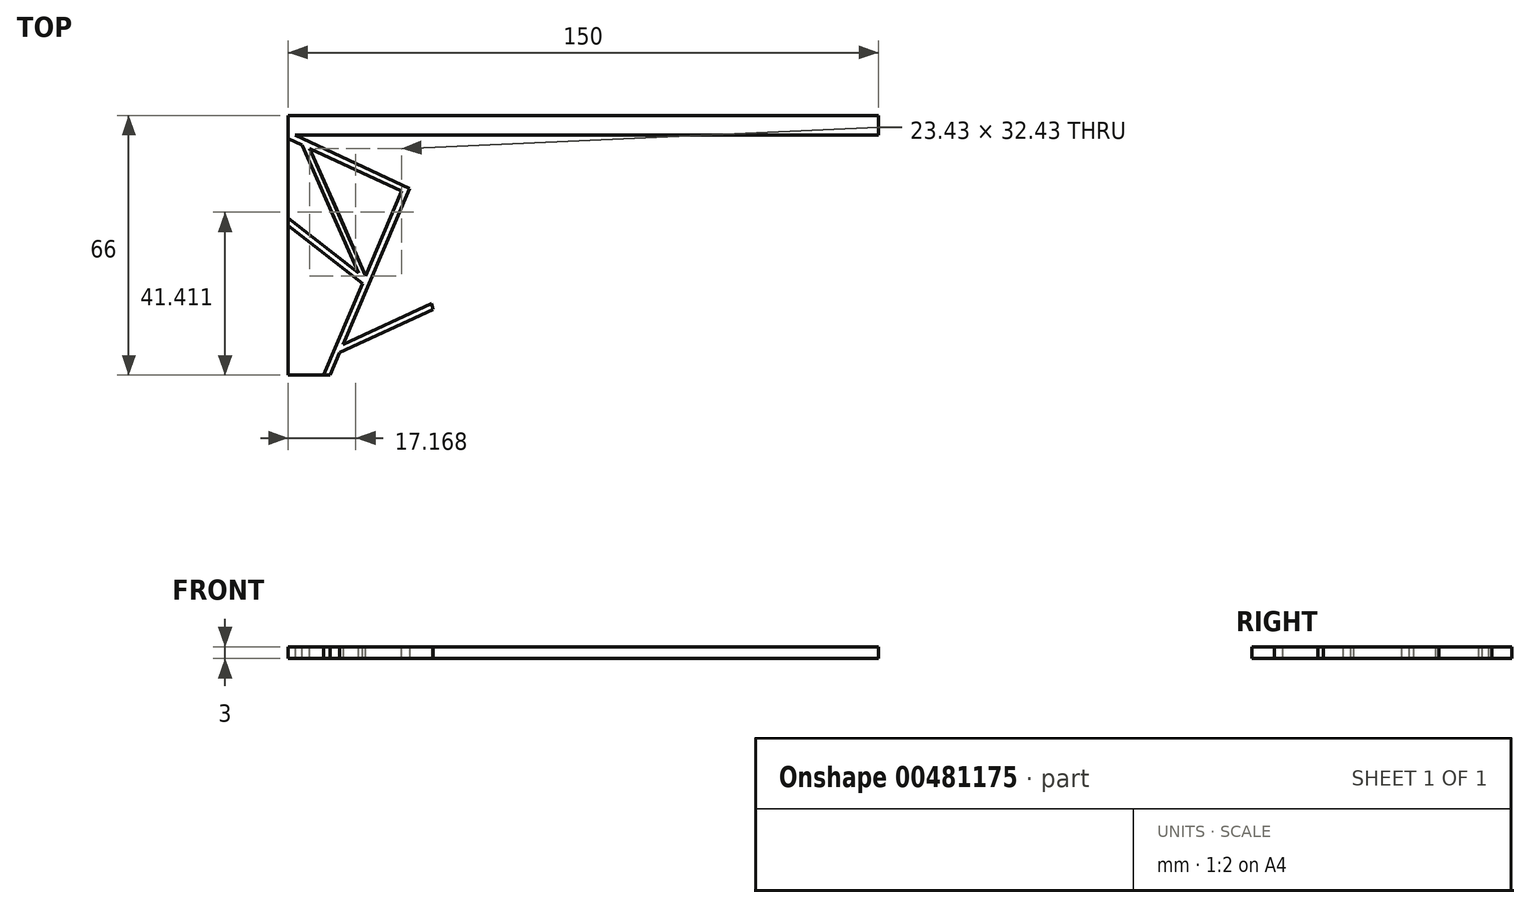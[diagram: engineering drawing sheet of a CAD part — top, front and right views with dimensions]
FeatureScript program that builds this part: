
annotation { "Feature Type Name" : "Feature", "Feature Type Description" : "" }
export const myFeature = defineFeature(function(context is Context, id is Id, definition is map)
    precondition{}
    {
        {
            var Q0;
            Q0=qCreatedBy(makeId("Top.planeOp"),FACE);
            var sketch = newSketch(context, id + "F0", { "sketchPlane" : qUnion([Q0])});
            skLineSegment(sketch, "E0", {"start": v(-52.18, 35.99) * mm, "end": v(-52.18, -44.01) * mm});
            skLineSegment(sketch, "E1", {"start": v(-52.18, -44.01) * mm, "end": v(27.82, -44.01) * mm});
            skLineSegment(sketch, "E2.bottom", {"start": v(-52.18, 35.99) * mm, "end": v(107.82, 35.99) * mm});
            skLineSegment(sketch, "E2.top", {"start": v(-52.18, -44.01) * mm, "end": v(107.82, -44.01) * mm});
            skLineSegment(sketch, "E2.right", {"start": v(107.82, 35.99) * mm, "end": v(107.82, -44.01) * mm});
            skLineSegment(sketch, "E3", {"start": v(-52.18, 35.99) * mm, "end": v(-52.18, 26.99) * mm});
            skLineSegment(sketch, "E4", {"start": v(-52.18, 26.99) * mm, "end": v(107.82, 26.99) * mm});
            skLineSegment(sketch, "E5.bottom", {"start": v(-52.18, 26.99) * mm, "end": v(-47.18, 26.99) * mm});
            skLineSegment(sketch, "E5.top", {"start": v(-52.18, -44.01) * mm, "end": v(-47.18, -44.01) * mm});
            skLineSegment(sketch, "E5.left", {"start": v(-52.18, 26.99) * mm, "end": v(-52.18, -44.01) * mm});
            skLineSegment(sketch, "E5.right", {"start": v(-47.18, 26.99) * mm, "end": v(-47.18, -44.01) * mm});
            skLineSegment(sketch, "E6.bottom", {"start": v(107.82, 26.99) * mm, "end": v(102.82, 26.99) * mm});
            skLineSegment(sketch, "E6.top", {"start": v(107.82, -44.01) * mm, "end": v(102.82, -44.01) * mm});
            skLineSegment(sketch, "E6.left", {"start": v(107.82, 26.99) * mm, "end": v(107.82, -44.01) * mm});
            skLineSegment(sketch, "E6.right", {"start": v(102.82, 26.99) * mm, "end": v(102.82, -44.01) * mm});
            skLineSegment(sketch, "E7.top", {"start": v(-52.18, 21.99) * mm, "end": v(107.82, 21.99) * mm});
            skLineSegment(sketch, "E7.left", {"start": v(-52.18, 26.99) * mm, "end": v(-52.18, 21.99) * mm});
            skLineSegment(sketch, "E7.right", {"start": v(107.82, 26.99) * mm, "end": v(107.82, 21.99) * mm});
            skLineSegment(sketch, "E8.top", {"start": v(-52.18, -39.01) * mm, "end": v(107.82, -39.01) * mm});
            skLineSegment(sketch, "E8.left", {"start": v(-52.18, -44.01) * mm, "end": v(-52.18, -39.01) * mm});
            skLineSegment(sketch, "E8.right", {"start": v(107.82, -44.01) * mm, "end": v(107.82, -39.01) * mm});
            skLineSegment(sketch, "E9", {"start": v(-47.18, 21.99) * mm, "end": v(0, 0) * mm});
            skLineSegment(sketch, "E10", {"start": v(0, 0) * mm, "end": v(11.28, 21.99) * mm});
            skLineSegment(sketch, "E11", {"start": v(11.28, 21.99) * mm, "end": v(23.62, -10.68) * mm});
            skLineSegment(sketch, "E12", {"start": v(23.62, -10.68) * mm, "end": v(-8.56, -30.37) * mm});
            skLineSegment(sketch, "E13", {"start": v(-8.56, -30.37) * mm, "end": v(-17.33, 8.07) * mm});
            skLineSegment(sketch, "E14", {"start": v(-17.33, 8.07) * mm, "end": v(-37.35, -39.01) * mm});
            skLineSegment(sketch, "E15", {"start": v(-37.35, -39.01) * mm, "end": v(42.87, -39.01) * mm});
            skLineSegment(sketch, "E16", {"start": v(42.87, -39.01) * mm, "end": v(7.53, -20.53) * mm});
            skLineSegment(sketch, "E17", {"start": v(102.82, -20.53) * mm, "end": v(74.6, 0) * mm});
            skLineSegment(sketch, "E18", {"start": v(74.6, 0) * mm, "end": v(42.87, -39.01) * mm});
            skLineSegment(sketch, "E19", {"start": v(57.9, -20.53) * mm, "end": v(31.89, 21.99) * mm});
            skLineSegment(sketch, "E20", {"start": v(31.89, 21.99) * mm, "end": v(45.34, 0) * mm});
            skLineSegment(sketch, "E21", {"start": v(45.34, 0) * mm, "end": v(95.17, 21.99) * mm});
            skLineSegment(sketch, "E22", {"start": v(95.17, 21.99) * mm, "end": v(86.96, -9) * mm});
            skPoint(sketch, "E23.endSnap0", {"position": v(38.62, 11) * mm});
            skLineSegment(sketch, "E24", {"start": v(75, -20.53) * mm, "end": v(81.37, -30.93) * mm});
            skLineSegment(sketch, "E25", {"start": v(81.37, -30.93) * mm, "end": v(96.81, -39.01) * mm});
            skLineSegment(sketch, "E26", {"start": v(-27.34, -15.47) * mm, "end": v(-47.18, 0) * mm});
            skLineSegment(sketch, "E27", {"start": v(-23.59, 11) * mm, "end": v(-23.27, 11.67) * mm});
            skLineSegment(sketch, "E28", {"start": v(-23.59, 11) * mm, "end": v(-23.9, 10.31) * mm});
            skLineSegment(sketch, "E29", {"start": v(-23.27, 11.67) * mm, "end": v(-45.4, 21.99) * mm});
            skLineSegment(sketch, "E30", {"start": v(-23.9, 10.31) * mm, "end": v(-47.18, 21.16) * mm});
            skLineSegment(sketch, "E31", {"start": v(-23.9, 10.31) * mm, "end": v(0, -0.83) * mm});
            skLineSegment(sketch, "E32", {"start": v(-23.27, 11.67) * mm, "end": v(0.34, 0.67) * mm});
            skLineSegment(sketch, "E33", {"start": v(-22.37, -3.79) * mm, "end": v(-23.05, -3.47) * mm});
            skLineSegment(sketch, "E34", {"start": v(-22.37, -3.79) * mm, "end": v(-21.68, -4.08) * mm});
            skLineSegment(sketch, "E35", {"start": v(-23.05, -3.47) * mm, "end": v(-17.71, 9.08) * mm});
            skLineSegment(sketch, "E36", {"start": v(-21.68, -4.08) * mm, "end": v(-16.35, 8.45) * mm});
            skLineSegment(sketch, "E37", {"start": v(-21.68, -4.08) * mm, "end": v(-36.54, -39.01) * mm});
            skLineSegment(sketch, "E38", {"start": v(-23.05, -3.47) * mm, "end": v(-38.17, -39.01) * mm});
            skLineSegment(sketch, "E39", {"start": v(-37.26, -7.73) * mm, "end": v(-36.8, -7.14) * mm});
            skLineSegment(sketch, "E40", {"start": v(-37.26, -7.73) * mm, "end": v(-37.72, -8.33) * mm});
            skLineSegment(sketch, "E41", {"start": v(-36.8, -7.14) * mm, "end": v(-47.18, 0.95) * mm});
            skLineSegment(sketch, "E42", {"start": v(-47.18, 0.95) * mm, "end": v(-27.04, -14.75) * mm});
            skLineSegment(sketch, "E43", {"start": v(-37.72, -8.33) * mm, "end": v(-47.18, -0.95) * mm});
            skLineSegment(sketch, "E44", {"start": v(-37.72, -8.33) * mm, "end": v(-28.26, -15.7) * mm});
            skLineSegment(sketch, "E45", {"start": v(-8.56, -39.01) * mm, "end": v(-8.56, -30.37) * mm});
            skLineSegment(sketch, "E46", {"start": v(81.37, -30.93) * mm, "end": v(64.21, -39.01) * mm});
            skLineSegment(sketch, "E47", {"start": v(63.35, 21.99) * mm, "end": v(66.4, 9.29) * mm});
            skLineSegment(sketch, "E48", {"start": v(64.21, -39.01) * mm, "end": v(51.37, -28.56) * mm});
            skLineSegment(sketch, "E49", {"start": v(-33.66, -32.25) * mm, "end": v(-10.57, -21.53) * mm});
            skLineSegment(sketch, "E50", {"start": v(57.9, -20.53) * mm, "end": v(17.7, -14.3) * mm});
            skLineSegment(sketch, "E51", {"start": v(75, -20.53) * mm, "end": v(82.14, -5.48) * mm});
            skLineSegment(sketch, "E52", {"start": v(82.14, -5.48) * mm, "end": v(75, -20.53) * mm});
            skLineSegment(sketch, "E53", {"start": v(75, -20.53) * mm, "end": v(102.82, -28.16) * mm});
            skLineSegment(sketch, "E54", {"start": v(-22.12, -26.89) * mm, "end": v(-22.43, -26.2) * mm});
            skLineSegment(sketch, "E55", {"start": v(-22.43, -26.2) * mm, "end": v(-10.74, -20.78) * mm});
            skLineSegment(sketch, "E56", {"start": v(-22.43, -26.2) * mm, "end": v(-33.22, -31.22) * mm});
            skLineSegment(sketch, "E57", {"start": v(-22.12, -26.89) * mm, "end": v(-21.8, -27.57) * mm});
            skLineSegment(sketch, "E58", {"start": v(-21.8, -27.57) * mm, "end": v(-10.4, -22.28) * mm});
            skLineSegment(sketch, "E59", {"start": v(-21.8, -27.57) * mm, "end": v(-34.1, -33.28) * mm});
            skLineSegment(sketch, "E60", {"start": v(75, -20.53) * mm, "end": v(67.3, -8.98) * mm});
            skLineSegment(sketch, "E61", {"start": v(18.1, 3.95) * mm, "end": v(38.62, 11) * mm});
            skLineSegment(sketch, "E62", {"start": v(7.53, -20.53) * mm, "end": v(0, 0) * mm});
            skLineSegment(sketch, "E63", {"start": v(-16.35, 8.45) * mm, "end": v(0, 21.99) * mm});
            skLineSegment(sketch, "E64", {"start": v(-17.71, 9.08) * mm, "end": v(-2.13, 21.99) * mm});
            skLineSegment(sketch, "E65", {"start": v(0, -0.83) * mm, "end": v(0.37, -1.02) * mm});
            skLineSegment(sketch, "E66", {"start": v(-42.76, 19.1) * mm, "end": v(-27.34, -15.47) * mm});
            skLineSegment(sketch, "E67", {"start": v(-35.05, 1.82) * mm, "end": v(-34.35, 2.07) * mm});
            skLineSegment(sketch, "E68", {"start": v(-34.35, 2.07) * mm, "end": v(-27.45, -13.82) * mm});
            skLineSegment(sketch, "E69", {"start": v(-34.35, 2.07) * mm, "end": v(-41.73, 18.62) * mm});
            skLineSegment(sketch, "E70", {"start": v(-35.05, 1.82) * mm, "end": v(-35.73, 1.51) * mm});
            skLineSegment(sketch, "E71", {"start": v(-35.73, 1.51) * mm, "end": v(-43.67, 19.69) * mm});
            skLineSegment(sketch, "E72", {"start": v(-35.73, 1.51) * mm, "end": v(-29.25, -13.03) * mm});
            skSolve(sketch);
        }
        {
            var Q0;
            {var subQ4=sQuery(id+"F0.wireOp",EDGE,"E27");Q0=makeQuery(id+"F0.imprint","IMPRINT",FACE,{"disambiguationData":[TD([[makeQuery(id+"F0.imprint","IMPRINT",EDGE,{"derivedFrom":subQ4}),1.0]])]});}
            var Q1;
            {var subQ1=sQuery(id+"F0.wireOp",EDGE,"E28");Q1=makeQuery(id+"F0.imprint","IMPRINT",FACE,{"disambiguationData":[TD([[makeQuery(id+"F0.imprint","IMPRINT",EDGE,{"derivedFrom":subQ1}),-1.0]])]});}
            var Q2;
            {var subQ4=sQuery(id+"F0.wireOp",EDGE,"E67");Q2=makeQuery(id+"F0.imprint","IMPRINT",FACE,{"disambiguationData":[TD([[makeQuery(id+"F0.imprint","IMPRINT",EDGE,{"derivedFrom":subQ4}),1.0]])]});}
            var Q3;
            {var subQ5=sQuery(id+"F0.wireOp",EDGE,"E70");Q3=makeQuery(id+"F0.imprint","IMPRINT",FACE,{"disambiguationData":[TD([[makeQuery(id+"F0.imprint","IMPRINT",EDGE,{"derivedFrom":subQ5}),-1.0]])]});}
            var Q4;
            {var subQ0=sQuery(id+"F0.wireOp",EDGE,"E27");Q4=makeQuery(id+"F0.imprint","IMPRINT",FACE,{"disambiguationData":[TD([[makeQuery(id+"F0.imprint","IMPRINT",EDGE,{"derivedFrom":subQ0}),-1.0]])]});}
            var Q5;
            {var subQ0=sQuery(id+"F0.wireOp",EDGE,"E28");Q5=makeQuery(id+"F0.imprint","IMPRINT",FACE,{"disambiguationData":[TD([[makeQuery(id+"F0.imprint","IMPRINT",EDGE,{"derivedFrom":subQ0}),1.0]])]});}
            var Q6;
            {var subQ0=sQuery(id+"F0.wireOp",EDGE,"E35");var subQ3=sQuery(id+"F0.wireOp",EDGE,"E9");var subQ4=makeQuery(id+"F0.imprint","INTERSECT",VERTEX,{"derivedFrom":[subQ3,subQ0]});Q6=makeQuery(id+"F0.imprint","IMPRINT",FACE,{"disambiguationData":[TD([[makeQuery(id+"F0.imprint","IMPRINT",EDGE,{"disambiguationData":[TD([[subQ4,-1.0]])],"derivedFrom":subQ3}),1.0]])]});}
            var Q7;
            {var subQ0=sQuery(id+"F0.wireOp",EDGE,"E14");var subQ5=sQuery(id+"F0.wireOp",EDGE,"E31");var subQ6=makeQuery(id+"F0.imprint","INTERSECT",VERTEX,{"derivedFrom":[subQ0,subQ5]});Q7=makeQuery(id+"F0.imprint","IMPRINT",FACE,{"disambiguationData":[TD([[makeQuery(id+"F0.imprint","IMPRINT",EDGE,{"disambiguationData":[TD([[subQ6,1.0]])],"derivedFrom":subQ5}),1.0]])]});}
            var Q8;
            {var subQ0=sQuery(id+"F0.wireOp",EDGE,"E13");var subQ5=sQuery(id+"F0.wireOp",EDGE,"E31");var subQ6=makeQuery(id+"F0.imprint","INTERSECT",VERTEX,{"derivedFrom":[subQ0,subQ5]});Q8=makeQuery(id+"F0.imprint","IMPRINT",FACE,{"disambiguationData":[TD([[makeQuery(id+"F0.imprint","IMPRINT",EDGE,{"disambiguationData":[TD([[subQ6,-1.0]])],"derivedFrom":subQ5}),1.0]])]});}
            var Q9;
            {var subQ1=sQuery(id+"F0.wireOp",EDGE,"E13");var subQ3=sQuery(id+"F0.wireOp",EDGE,"E31");var subQ4=makeQuery(id+"F0.imprint","INTERSECT",VERTEX,{"derivedFrom":[subQ1,subQ3]});Q9=makeQuery(id+"F0.imprint","IMPRINT",FACE,{"disambiguationData":[TD([[makeQuery(id+"F0.imprint","IMPRINT",EDGE,{"disambiguationData":[TD([[subQ4,1.0]])],"derivedFrom":subQ3}),1.0]])]});}
            var Q10;
            {var subQ6=sQuery(id+"F0.wireOp",EDGE,"E34");Q10=makeQuery(id+"F0.imprint","IMPRINT",FACE,{"disambiguationData":[TD([[makeQuery(id+"F0.imprint","IMPRINT",EDGE,{"derivedFrom":subQ6}),1.0]])]});}
            var Q11;
            {var subQ0=sQuery(id+"F0.wireOp",EDGE,"E33");Q11=makeQuery(id+"F0.imprint","IMPRINT",FACE,{"disambiguationData":[TD([[makeQuery(id+"F0.imprint","IMPRINT",EDGE,{"derivedFrom":subQ0}),-1.0]])]});}
            var Q12;
            {var subQ0=sQuery(id+"F0.wireOp",EDGE,"E36");var subQ1=sQuery(id+"F0.wireOp",EDGE,"E13");var subQ2=makeQuery(id+"F0.imprint","INTERSECT",VERTEX,{"derivedFrom":[subQ1,subQ0]});Q12=makeQuery(id+"F0.imprint","IMPRINT",FACE,{"disambiguationData":[TD([[makeQuery(id+"F0.imprint","IMPRINT",EDGE,{"disambiguationData":[TD([[subQ2,-1.0]])],"derivedFrom":subQ1}),-1.0]])]});}
            var Q13;
            {var subQ7=sQuery(id+"F0.wireOp",EDGE,"E34");Q13=makeQuery(id+"F0.imprint","IMPRINT",FACE,{"disambiguationData":[TD([[makeQuery(id+"F0.imprint","IMPRINT",EDGE,{"derivedFrom":subQ7}),-1.0]])]});}
            var Q14;
            {var subQ6=sQuery(id+"F0.wireOp",EDGE,"E33");Q14=makeQuery(id+"F0.imprint","IMPRINT",FACE,{"disambiguationData":[TD([[makeQuery(id+"F0.imprint","IMPRINT",EDGE,{"derivedFrom":subQ6}),1.0]])]});}
            var Q15;
            {var subQ0=sQuery(id+"F0.wireOp",EDGE,"E67");Q15=makeQuery(id+"F0.imprint","IMPRINT",FACE,{"disambiguationData":[TD([[makeQuery(id+"F0.imprint","IMPRINT",EDGE,{"derivedFrom":subQ0}),-1.0]])]});}
            var Q16;
            {var subQ4=sQuery(id+"F0.wireOp",EDGE,"E70");Q16=makeQuery(id+"F0.imprint","IMPRINT",FACE,{"disambiguationData":[TD([[makeQuery(id+"F0.imprint","IMPRINT",EDGE,{"derivedFrom":subQ4}),1.0]])]});}
            var Q17;
            {var subQ5=sQuery(id+"F0.wireOp",EDGE,"E39");Q17=makeQuery(id+"F0.imprint","IMPRINT",FACE,{"disambiguationData":[TD([[makeQuery(id+"F0.imprint","IMPRINT",EDGE,{"derivedFrom":subQ5}),1.0]])]});}
            var Q18;
            {var subQ4=sQuery(id+"F0.wireOp",EDGE,"E40");Q18=makeQuery(id+"F0.imprint","IMPRINT",FACE,{"disambiguationData":[TD([[makeQuery(id+"F0.imprint","IMPRINT",EDGE,{"derivedFrom":subQ4}),-1.0]])]});}
            var Q19;
            {var subQ1=sQuery(id+"F0.wireOp",EDGE,"E39");Q19=makeQuery(id+"F0.imprint","IMPRINT",FACE,{"disambiguationData":[TD([[makeQuery(id+"F0.imprint","IMPRINT",EDGE,{"derivedFrom":subQ1}),-1.0]])]});}
            var Q20;
            {var subQ0=sQuery(id+"F0.wireOp",EDGE,"E40");Q20=makeQuery(id+"F0.imprint","IMPRINT",FACE,{"disambiguationData":[TD([[makeQuery(id+"F0.imprint","IMPRINT",EDGE,{"derivedFrom":subQ0}),1.0]])]});}
            var Q21;
            {var subQ4=sQuery(id+"F0.wireOp",EDGE,"E57");Q21=makeQuery(id+"F0.imprint","IMPRINT",FACE,{"disambiguationData":[TD([[makeQuery(id+"F0.imprint","IMPRINT",EDGE,{"derivedFrom":subQ4}),-1.0]])]});}
            var Q22;
            {var subQ4=sQuery(id+"F0.wireOp",EDGE,"E54");Q22=makeQuery(id+"F0.imprint","IMPRINT",FACE,{"disambiguationData":[TD([[makeQuery(id+"F0.imprint","IMPRINT",EDGE,{"derivedFrom":subQ4}),1.0]])]});}
            var Q23;
            {var subQ4=sQuery(id+"F0.wireOp",EDGE,"E54");Q23=makeQuery(id+"F0.imprint","IMPRINT",FACE,{"disambiguationData":[TD([[makeQuery(id+"F0.imprint","IMPRINT",EDGE,{"derivedFrom":subQ4}),-1.0]])]});}
            var Q24;
            {var subQ4=sQuery(id+"F0.wireOp",EDGE,"E57");Q24=makeQuery(id+"F0.imprint","IMPRINT",FACE,{"disambiguationData":[TD([[makeQuery(id+"F0.imprint","IMPRINT",EDGE,{"derivedFrom":subQ4}),1.0]])]});}
            var Q25;
            {var subQ3=sQuery(id+"F0.wireOp",EDGE,"E42");var subQ5=sQuery(id+"F0.wireOp",EDGE,"E38");var subQ6=makeQuery(id+"F0.imprint","INTERSECT",VERTEX,{"derivedFrom":[subQ5,subQ3]});Q25=makeQuery(id+"F0.imprint","IMPRINT",FACE,{"disambiguationData":[TD([[makeQuery(id+"F0.imprint","IMPRINT",EDGE,{"disambiguationData":[TD([[subQ6,-1.0]])],"derivedFrom":subQ5}),1.0]])]});}
            var Q26;
            {var subQ1=sQuery(id+"F0.wireOp",EDGE,"E26");var subQ3=sQuery(id+"F0.wireOp",EDGE,"E38");var subQ4=makeQuery(id+"F0.imprint","INTERSECT",VERTEX,{"derivedFrom":[subQ1,subQ3]});Q26=makeQuery(id+"F0.imprint","IMPRINT",FACE,{"disambiguationData":[TD([[makeQuery(id+"F0.imprint","IMPRINT",EDGE,{"disambiguationData":[TD([[subQ4,1.0]])],"derivedFrom":subQ3}),1.0]])]});}
            var Q27;
            {var subQ0=sQuery(id+"F0.wireOp",EDGE,"E38");var subQ1=makeQuery(id+"F0.imprint","INTERSECT",VERTEX,{"derivedFrom":[subQ0,sQuery(id+"F0.wireOp",EDGE,"E44")]});Q27=makeQuery(id+"F0.imprint","IMPRINT",FACE,{"disambiguationData":[TD([[makeQuery(id+"F0.imprint","IMPRINT",EDGE,{"disambiguationData":[TD([[subQ1,1.0]])],"derivedFrom":subQ0}),1.0]])]});}
            var Q28;
            {var subQ0=sQuery(id+"F0.wireOp",EDGE,"E42");var subQ1=sQuery(id+"F0.wireOp",EDGE,"E38");var subQ2=makeQuery(id+"F0.imprint","INTERSECT",VERTEX,{"derivedFrom":[subQ1,subQ0]});Q28=makeQuery(id+"F0.imprint","IMPRINT",FACE,{"disambiguationData":[TD([[makeQuery(id+"F0.imprint","IMPRINT",EDGE,{"disambiguationData":[TD([[subQ2,-1.0]])],"derivedFrom":subQ1}),-1.0]])]});}
            var Q29;
            {var subQ9=sQuery(id+"F0.wireOp",EDGE,"E2.top");var subQ12=sQuery(id+"F0.wireOp",EDGE,"E5.right");var subQ13=makeQuery(id+"F0.imprint","INTERSECT",VERTEX,{"derivedFrom":[subQ12,subQ9]});Q29=makeQuery(id+"F0.imprint","IMPRINT",FACE,{"disambiguationData":[TD([[makeQuery(id+"F0.imprint","IMPRINT",EDGE,{"disambiguationData":[TD([[subQ13,1.0]])],"derivedFrom":subQ12}),1.0]])]});}
            var Q30;
            {var subQ6=sQuery(id+"F0.wireOp",EDGE,"E5.left");Q30=makeQuery(id+"F0.imprint","IMPRINT",FACE,{"disambiguationData":[TD([[makeQuery(id+"F0.imprint","IMPRINT",EDGE,{"derivedFrom":subQ6}),1.0]])]});}
            var Q31;
            {var subQ5=sQuery(id+"F0.wireOp",EDGE,"E8.left");Q31=makeQuery(id+"F0.imprint","IMPRINT",FACE,{"disambiguationData":[TD([[makeQuery(id+"F0.imprint","IMPRINT",EDGE,{"derivedFrom":subQ5}),-1.0]])]});}
            var Q32;
            {var subQ3=sQuery(id+"F0.wireOp",EDGE,"E4");var subQ12=sQuery(id+"F0.wireOp",EDGE,"E6.right");var subQ13=makeQuery(id+"F0.imprint","INTERSECT",VERTEX,{"derivedFrom":[subQ12,subQ3]});Q32=makeQuery(id+"F0.imprint","IMPRINT",FACE,{"disambiguationData":[TD([[makeQuery(id+"F0.imprint","IMPRINT",EDGE,{"disambiguationData":[TD([[subQ13,-1.0]])],"derivedFrom":subQ12}),-1.0]])]});}
            var Q33;
            {var subQ7=sQuery(id+"F0.wireOp",EDGE,"E6.left");Q33=makeQuery(id+"F0.imprint","IMPRINT",FACE,{"disambiguationData":[TD([[makeQuery(id+"F0.imprint","IMPRINT",EDGE,{"derivedFrom":subQ7}),-1.0]])]});}
            var Q34;
            {var subQ5=sQuery(id+"F0.wireOp",EDGE,"E8.right");Q34=makeQuery(id+"F0.imprint","IMPRINT",FACE,{"disambiguationData":[TD([[makeQuery(id+"F0.imprint","IMPRINT",EDGE,{"derivedFrom":subQ5}),1.0]])]});}
            var Q35;
            {var subQ5=sQuery(id+"F0.wireOp",EDGE,"E7.right");Q35=makeQuery(id+"F0.imprint","IMPRINT",FACE,{"disambiguationData":[TD([[makeQuery(id+"F0.imprint","IMPRINT",EDGE,{"derivedFrom":subQ5}),-1.0]])]});}
            var Q36;
            {var subQ5=sQuery(id+"F0.wireOp",EDGE,"E7.left");Q36=makeQuery(id+"F0.imprint","IMPRINT",FACE,{"disambiguationData":[TD([[makeQuery(id+"F0.imprint","IMPRINT",EDGE,{"derivedFrom":subQ5}),1.0]])]});}
            extrude(context, id + "F1", {"entities" : qUnion([Q0, Q1, Q2, Q3, Q4, Q5, Q6, Q7, Q8, Q9, Q10, Q11, Q12, Q13, Q14, Q15, Q16, Q17, Q18, Q19, Q20, Q21, Q22, Q23, Q24, Q25, Q26, Q27, Q28, Q29, Q30, Q31, Q32, Q33, Q34, Q35, Q36]), "depth" : 3 * mm});
        }
        {
            var Q0;
            Q0=makeQuery(id+"F1.opExtrude","CAP_FACE",FACE,{"disambiguationData":[OSD([sQuery(id+"F0.wireOp",EDGE,"E5.left"),sQuery(id+"F0.wireOp",EDGE,"E5.right"),sQuery(id+"F0.wireOp",EDGE,"E6.left"),sQuery(id+"F0.wireOp",EDGE,"E6.right"),sQuery(id+"F0.wireOp",EDGE,"E4"),sQuery(id+"F0.wireOp",EDGE,"E7.top"),sQuery(id+"F0.wireOp",EDGE,"E7.left"),sQuery(id+"F0.wireOp",EDGE,"E7.right"),sQuery(id+"F0.wireOp",EDGE,"E2.top"),sQuery(id+"F0.wireOp",EDGE,"E8.top"),sQuery(id+"F0.wireOp",EDGE,"E8.left"),sQuery(id+"F0.wireOp",EDGE,"E8.right"),sQuery(id+"F0.wireOp",EDGE,"E13"),sQuery(id+"F0.wireOp",EDGE,"E15"),sQuery(id+"F0.wireOp",EDGE,"E29"),sQuery(id+"F0.wireOp",EDGE,"E30"),sQuery(id+"F0.wireOp",EDGE,"E31"),sQuery(id+"F0.wireOp",EDGE,"E32"),sQuery(id+"F0.wireOp",EDGE,"E35"),sQuery(id+"F0.wireOp",EDGE,"E36"),sQuery(id+"F0.wireOp",EDGE,"E37"),sQuery(id+"F0.wireOp",EDGE,"E38"),sQuery(id+"F0.wireOp",EDGE,"E42"),sQuery(id+"F0.wireOp",EDGE,"E43"),sQuery(id+"F0.wireOp",EDGE,"E44"),sQuery(id+"F0.wireOp",EDGE,"E55"),sQuery(id+"F0.wireOp",EDGE,"E56"),sQuery(id+"F0.wireOp",EDGE,"E58"),sQuery(id+"F0.wireOp",EDGE,"E59"),sQuery(id+"F0.wireOp",EDGE,"E68"),sQuery(id+"F0.wireOp",EDGE,"E69"),sQuery(id+"F0.wireOp",EDGE,"E71"),sQuery(id+"F0.wireOp",EDGE,"E72")])],"isStart":false});
            var sketch = newSketch(context, id + "F2", { "sketchPlane" : qUnion([Q0])});
            skLineSegment(sketch, "E73", {"start": v(-41.73, 18.62) * mm, "end": v(-18.3, 7.7) * mm});
            skLineSegment(sketch, "E74", {"start": v(-18.3, 7.7) * mm, "end": v(-27.45, -13.82) * mm});
            skLineSegment(sketch, "E75", {"start": v(-27.45, -13.82) * mm, "end": v(-41.73, 18.62) * mm});
            skLineSegment(sketch, "E76", {"start": v(-43.58, 19.48) * mm, "end": v(-29.25, -13.03) * mm});
            skLineSegment(sketch, "E77", {"start": v(-29.25, -13.03) * mm, "end": v(-47.18, 0.95) * mm});
            skLineSegment(sketch, "E78", {"start": v(-47.18, 0.95) * mm, "end": v(-47.18, 21.16) * mm});
            skLineSegment(sketch, "E79", {"start": v(-47.18, 21.16) * mm, "end": v(-43.58, 19.48) * mm});
            skLineSegment(sketch, "E80", {"start": v(-28.26, -15.7) * mm, "end": v(-47.18, -0.95) * mm});
            skLineSegment(sketch, "E81", {"start": v(-47.18, -0.95) * mm, "end": v(-47.18, -39.01) * mm});
            skLineSegment(sketch, "E82", {"start": v(-47.18, -39.01) * mm, "end": v(-38.17, -39.01) * mm});
            skLineSegment(sketch, "E83", {"start": v(-38.17, -39.01) * mm, "end": v(-28.26, -15.7) * mm});
            skSolve(sketch);
        }
        {
            var Q0;
            Q0 = qSketchRegion(id + "F2", true);
            extrude(context, id + "F3", {"entities" : qUnion([Q0]), "oppositeDirection" : true, "depth" : 3 * mm});
        }
    });
